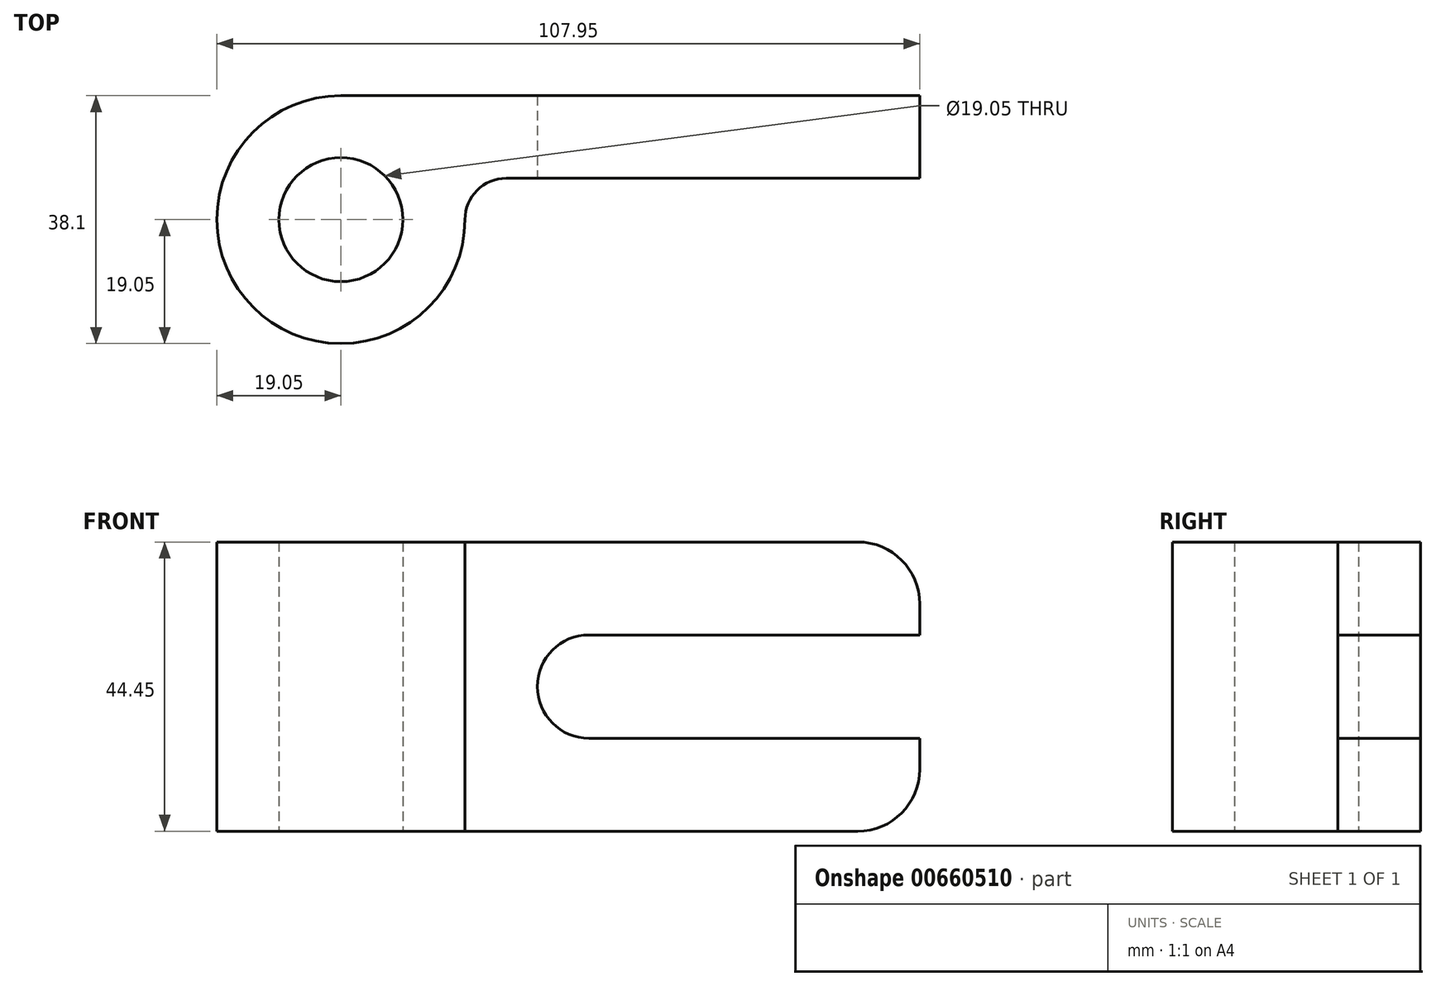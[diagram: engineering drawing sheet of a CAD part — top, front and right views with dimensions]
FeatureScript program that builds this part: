
annotation { "Feature Type Name" : "Feature", "Feature Type Description" : "" }
export const myFeature = defineFeature(function(context is Context, id is Id, definition is map)
    precondition{}
    {
        {
            var Q0;
            Q0=qCreatedBy(makeId("Top.planeOp"),FACE);
            var sketch = newSketch(context, id + "F0", { "sketchPlane" : qUnion([Q0])});
            skLineSegment(sketch, "E0", {"start": v(0, 0) * mm, "end": v(50.8, 0) * mm});
            skLineSegment(sketch, "E1", {"start": v(50.8, 0) * mm, "end": v(50.8, 12.7) * mm});
            skLineSegment(sketch, "E2", {"start": v(0, 0) * mm, "end": v(0, 12.7) * mm});
            skLineSegment(sketch, "E3", {"start": v(50.8, 12.7) * mm, "end": v(0, 12.7) * mm});
            skLineSegment(sketch, "E4", {"start": v(0, 12.7) * mm, "end": v(-38.1, 12.7) * mm});
            skCircle(sketch, "E5", {"center": v(-38.1, -6.35) * mm, "radius": 19.05 * mm});
            skCircle(sketch, "E6", {"center": v(-38.1, -6.35) * mm, "radius": 9.53 * mm});
            skLineSegment(sketch, "E7", {"start": v(0, 0) * mm, "end": v(-20.14, 0) * mm});
            skLineSegment(sketch, "E8", {"start": v(-38.1, -6.35) * mm, "end": v(-38.1, 23.4) * mm, "construction": true});
            skLineSegment(sketch, "E9", {"start": v(0, 0) * mm, "end": v(0, 25.47) * mm, "construction": true});
            skCircle(sketch, "E10", {"center": v(-12.7, -6.35) * mm, "radius": 6.35 * mm});
            skSolve(sketch);
        }
        {
            var Q0;
            Q0=makeQuery(id+"F0.imprint","IMPRINT",FACE,{"disambiguationData":[TD([[makeQuery(id+"F0.imprint","IMPRINT",EDGE,{"derivedFrom":sQuery(id+"F0.wireOp",EDGE,"E6")}),-1.0]])]});
            var Q1;
            {var subQ4=sQuery(id+"F0.wireOp",EDGE,"E2");Q1=makeQuery(id+"F0.imprint","IMPRINT",FACE,{"disambiguationData":[TD([[makeQuery(id+"F0.imprint","IMPRINT",EDGE,{"derivedFrom":subQ4}),1.0]])]});}
            var Q2;
            {var subQ0=sQuery(id+"F0.wireOp",EDGE,"E7");var subQ1=sQuery(id+"F0.wireOp",EDGE,"E5");var subQ2=makeQuery(id+"F0.imprint","INTERSECT",VERTEX,{"derivedFrom":[subQ1,subQ0]});Q2=makeQuery(id+"F0.imprint","IMPRINT",FACE,{"disambiguationData":[TD([[makeQuery(id+"F0.imprint","IMPRINT",EDGE,{"disambiguationData":[TD([[subQ2,1.0]])],"derivedFrom":subQ1}),-1.0]])]});}
            var Q3;
            Q3=makeQuery(id+"F0.imprint","IMPRINT",FACE,{"disambiguationData":[TD([[makeQuery(id+"F0.imprint","IMPRINT",EDGE,{"derivedFrom":sQuery(id+"F0.wireOp",EDGE,"E0")}),1.0]])]});
            extrude(context, id + "F1", {"entities" : qUnion([Q0, Q1, Q2, Q3]), "depth" : 44.45 * mm, "offsetDistance" : 25.4 * mm});
        }
        {
            var Q0;
            Q0=makeQuery(id+"F1.opExtrude","SWEPT_FACE",FACE,{"disambiguationData":[OSD([sQuery(id+"F0.wireOp",EDGE,"E0"),sQuery(id+"F0.wireOp",EDGE,"E7")])]});
            var sketch = newSketch(context, id + "F2", { "sketchPlane" : qUnion([Q0])});
            skLineSegment(sketch, "E11", {"start": v(50.8, 14.29) * mm, "end": v(0, 14.29) * mm});
            skLineSegment(sketch, "E12", {"start": v(0, 14.29) * mm, "end": v(0, 30.16) * mm});
            skLineSegment(sketch, "E13", {"start": v(0, 30.16) * mm, "end": v(50.8, 30.16) * mm});
            skLineSegment(sketch, "E14", {"start": v(50.8, 14.29) * mm, "end": v(50.8, 30.16) * mm});
            skCircle(sketch, "E15", {"center": v(0, 22.22) * mm, "radius": 7.94 * mm});
            skArc(sketch, "E16", {"start": v(49.52, 30.16) * mm, "mid": v(41.28, 44.45) * mm, "end": v(33.03, 30.16) * mm});
            skArc(sketch, "E17", {"start": v(33.03, 14.29) * mm, "mid": v(41.28, 0) * mm, "end": v(49.52, 14.29) * mm});
            skSolve(sketch);
        }
        {
            var Q0;
            {var subQ0=sQuery(id+"F2.wireOp",EDGE,"E12");Q0=makeQuery(id+"F2.imprint","IMPRINT",FACE,{"disambiguationData":[TD([[makeQuery(id+"F2.imprint","IMPRINT",EDGE,{"derivedFrom":subQ0}),1.0]])]});}
            var Q1;
            {var subQ0=sQuery(id+"F2.wireOp",EDGE,"E12");Q1=makeQuery(id+"F2.imprint","IMPRINT",FACE,{"disambiguationData":[TD([[makeQuery(id+"F2.imprint","IMPRINT",EDGE,{"derivedFrom":subQ0}),-1.0]])]});}
            var Q2;
            {var subQ0=sQuery(id+"F2.wireOp",EDGE,"E11");Q2=makeQuery(id+"F2.imprint","IMPRINT",FACE,{"disambiguationData":[TD([[makeQuery(id+"F2.imprint","IMPRINT",EDGE,{"derivedFrom":subQ0}),-1.0]])]});}
            var Q3;
            {var subQ0=sQuery(id+"F2.wireOp",EDGE,"E16");var subQ1=sQuery(id+"F0.wireOp",EDGE,"E0");var subQ2=makeQuery(id+"F1.opExtrude","SWEPT_EDGE",EDGE,{"disambiguationData":[OSD([subQ1,sQuery(id+"F0.wireOp",EDGE,"E1")])]});var subQ3=makeQuery(id+"F2.imprint","INTERSECT",VERTEX,{"derivedFrom":[subQ2,subQ0]});Q3=makeQuery(id+"F2.imprint","IMPRINT",FACE,{"disambiguationData":[TD([[makeQuery(id+"F2.imprint","IMPRINT",EDGE,{"disambiguationData":[TD([[subQ3,-1.0]])],"derivedFrom":subQ0}),-1.0]])]});}
            var Q4;
            {var subQ0=sQuery(id+"F2.wireOp",EDGE,"E17");var subQ1=sQuery(id+"F0.wireOp",EDGE,"E0");var subQ2=makeQuery(id+"F1.opExtrude","CAP_EDGE",EDGE,{"disambiguationData":[OSD([subQ1,sQuery(id+"F0.wireOp",EDGE,"E7")])],"isStart":true});var subQ3=makeQuery(id+"F2.imprint","INTERSECT",VERTEX,{"derivedFrom":[subQ2,subQ0]});Q4=makeQuery(id+"F2.imprint","IMPRINT",FACE,{"disambiguationData":[TD([[makeQuery(id+"F2.imprint","IMPRINT",EDGE,{"disambiguationData":[TD([[subQ3,-1.0]])],"derivedFrom":subQ0}),-1.0]])]});}
            extrude(context, id + "F3", {"entities" : qUnion([Q0, Q1, Q2, Q3, Q4]), "operationType" : NewBodyOperationType.REMOVE, "oppositeDirection" : true, "depth" : 12.7 * mm, "offsetDistance" : 25.4 * mm});
        }
    });
